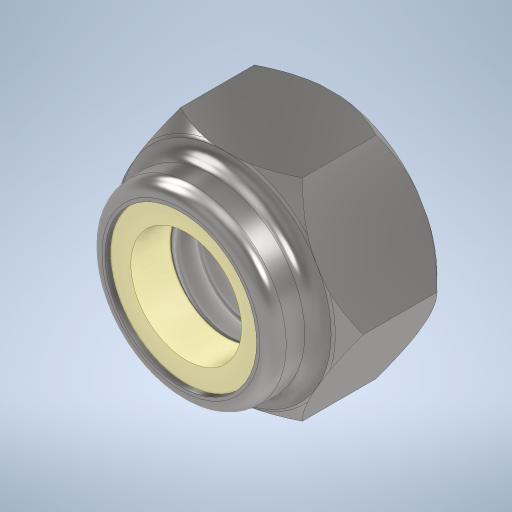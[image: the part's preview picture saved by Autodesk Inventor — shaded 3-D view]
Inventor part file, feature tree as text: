
AUTODESK INVENTOR PART (.ipt)
format: ipt  version: 2024 (Build 280153000, 153)  size: 398,848 bytes
history: native  units: mm
features: sketch x6, extrude x5, chamfer x2, hole x2, fillet x1, projected_geometry x1, other x1
ambient origin geometry x8: Origin, YZ Plane, XZ Plane, XY Plane, X Axis, Y Axis, Z Axis, Center Point
bodies: Solid1 (feature_tree)
feature tree (18):
  sketch  "Sketch1"  dims[d0=8.0mm d2=4.0mm d3=0.0mm d4=0.6mm d5=2.0mm d6=45.0deg]
  extrude  "Extrusion1"  Depth=4.0mm TaperAngle=0.0deg
  chamfer  "Chamfer1"  Distance=0.6mm Angle=45.0deg
  extrude  "Extrusion2"  Depth=7.0mm
  extrude  "Extrusion3"  Depth=0.5mm
  fillet  "Fillet1"  Radius=5.75mm
  extrude  "Extrusion4"  Depth=1.5mm TaperAngle=0.0deg
  extrude  "Extrusion5"  Depth=4.0mm TaperAngle=45.0deg
  hole  "Hole1"  [1 undecoded]
  hole  "Hole2"  [1 undecoded]
  chamfer  "Chamfer2"  [1 undecoded]
  sketch  "Sketch2"  dims[d7=0.0mm d8=0.0mm d9=7.0mm]
  sketch  "Sketch3"  dims[d10=1.7mm d11=0.0mm d12=0.5mm d13=5.75mm]
  sketch  "Sketch4"  dims[d14=1.7mm d15=0.0mm d16=1.5mm d17=0.0mm]
  projected_geometry  "Projected Loop1"
  other  "Lockring"
  sketch  "Sketch5"  dims[d18=4.134mm d19=10.0mm d20=4.0mm d21=2.0mm d22=90.0deg d23=11.8mm d24=0.0mm]
  sketch  "Sketch6"  dims[d25=4.2mm d26=8.0mm d27=4.0mm d28=2.0mm d29=90.0deg d30=8.0mm d31=0.0mm d32=0.25mm d33=2.0mm d34=45.0deg]
note: 3 required parameter values undecoded (feature->parameter linkage not recoverable at this tier; creation-order binding heuristic only, values carry confidence <= 0.55)
